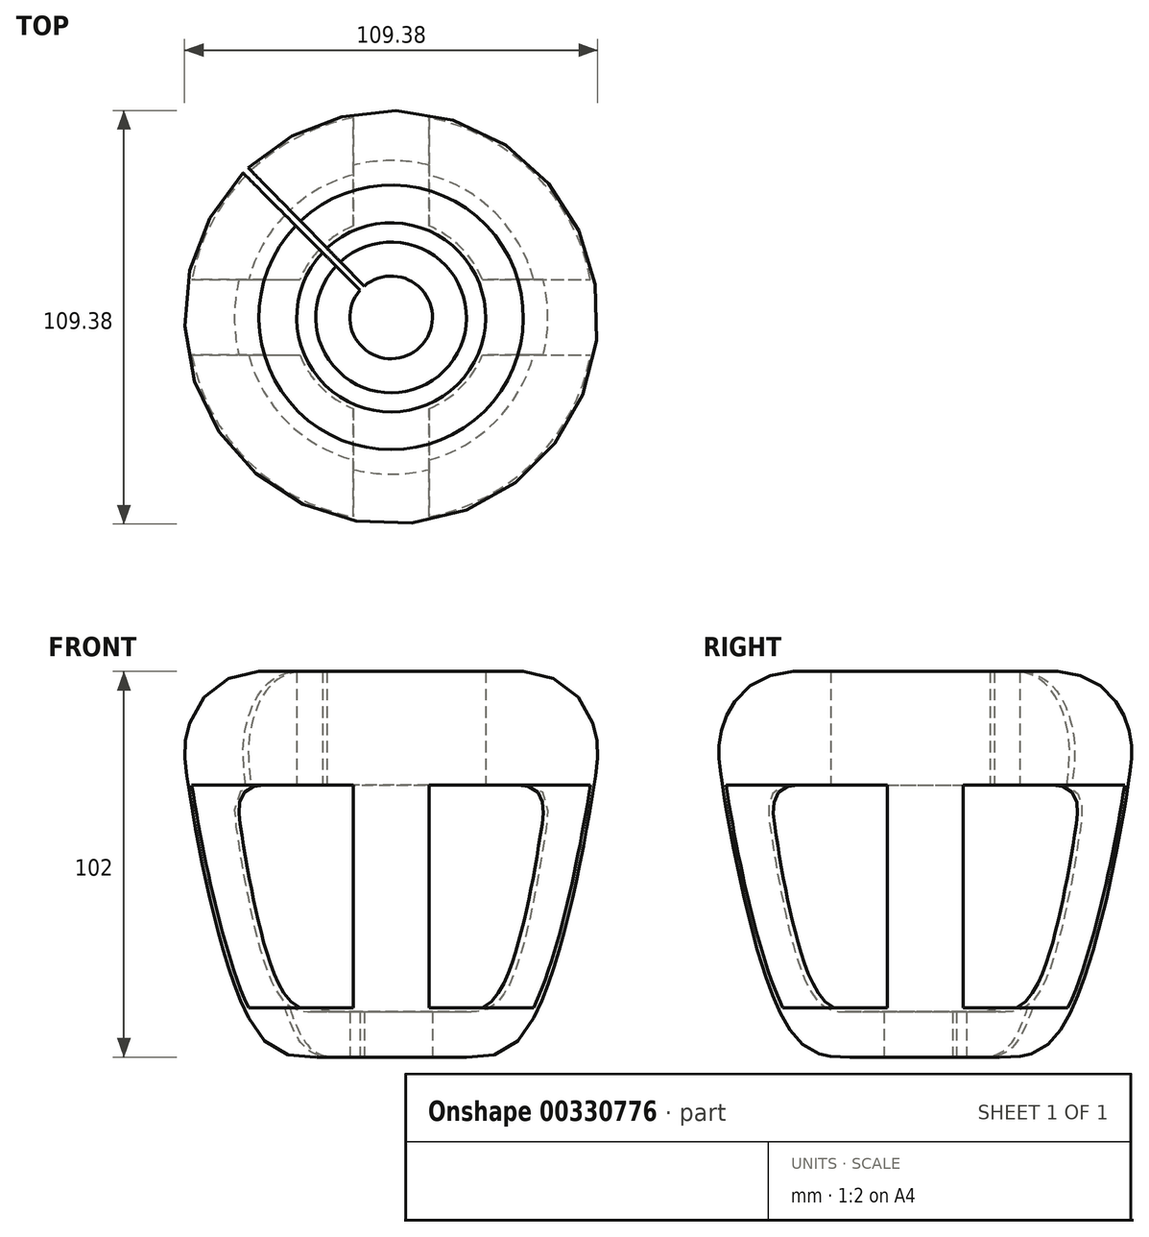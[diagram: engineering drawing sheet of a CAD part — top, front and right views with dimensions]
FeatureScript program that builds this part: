
annotation { "Feature Type Name" : "Feature", "Feature Type Description" : "" }
export const myFeature = defineFeature(function(context is Context, id is Id, definition is map)
    precondition{}
    {
        {
            var Q0;
            Q0=qCreatedBy(makeId("Front.planeOp"),FACE);
            var sketch = newSketch(context, id + "F0", { "sketchPlane" : qUnion([Q0])});
            skLineSegment(sketch, "E0", {"start": v(19.94, 0) * mm, "end": v(19.94, 12) * mm});
            skLineSegment(sketch, "E1", {"start": v(0, 12) * mm, "end": v(0, 72) * mm});
            skLineSegment(sketch, "E2", {"start": v(35, 72) * mm, "end": v(35, 102) * mm});
            skLineSegment(sketch, "E3", {"start": v(0, 0) * mm, "end": v(0, 122.17) * mm, "construction": true});
            skPoint(sketch, "E4.1.internal.snap0", {"position": v(35, 87) * mm});
            skPoint(sketch, "E4.3.internal.snap0", {"position": v(19.94, 6) * mm});
            skFitSpline(sketch, "E4", {"points": [v(35, 102) * mm, v(53.76, 87) * mm, v(53.7, 72) * mm, v(35, 6) * mm, v(19.94, 0) * mm], "startDerivative": vector(163.57, -9.42) * mm, "endDerivative": vector(-83.47, -0.77) * mm});
            skFitSpline(sketch, "E5", {"points": [v(35, 72) * mm, v(40.9, 59.77) * mm, v(37.46, 40.18) * mm, v(29.27, 15.77) * mm, v(19.94, 12) * mm], "startDerivative": vector(103.2, -2.48) * mm, "endDerivative": vector(-64.73, 3.98) * mm});
            skLineSegment(sketch, "E6", {"start": v(19.94, 12) * mm, "end": v(10.94, 12) * mm});
            skLineSegment(sketch, "E7", {"start": v(10.94, 12) * mm, "end": v(10.94, 0) * mm});
            skLineSegment(sketch, "E8", {"start": v(10.94, 0) * mm, "end": v(19.94, 0) * mm});
            skLineSegment(sketch, "E9", {"start": v(35, 102) * mm, "end": v(25, 102) * mm});
            skLineSegment(sketch, "E10", {"start": v(25, 102) * mm, "end": v(25, 72) * mm});
            skLineSegment(sketch, "E11", {"start": v(25, 72) * mm, "end": v(35, 72) * mm});
            skSolve(sketch);
        }
        {
            var Q0;
            Q0=makeQuery(id+"F0.imprint","IMPRINT",FACE,{"disambiguationData":[TD([[makeQuery(id+"F0.imprint","IMPRINT",EDGE,{"derivedFrom":sQuery(id+"F0.wireOp",EDGE,"E2")}),1.0]])]});
            var Q1;
            Q1=makeQuery(id+"F0.imprint","IMPRINT",FACE,{"disambiguationData":[TD([[makeQuery(id+"F0.imprint","IMPRINT",EDGE,{"derivedFrom":sQuery(id+"F0.wireOp",EDGE,"E0")}),-1.0]])]});
            var Q2;
            Q2=makeQuery(id+"F0.imprint","IMPRINT",FACE,{"disambiguationData":[TD([[makeQuery(id+"F0.imprint","IMPRINT",EDGE,{"derivedFrom":sQuery(id+"F0.wireOp",EDGE,"E0")}),1.0]])]});
            var Q3;
            Q3=sQuery(id+"F0.wireOp",EDGE,"E3");
            revolve(context, id + "F1", {"entities" : qUnion([Q0, Q1, Q2]), "axis" : qUnion([Q3]), "revolveType" : RevolveType.FULL});
        }
        {
            var Q0;
            Q0=qCreatedBy(makeId("Front.planeOp"),FACE);
            cPlane(context, id + "F2", {"entities" : qUnion([Q0]), "cplaneType" : CPlaneType.OFFSET, "offset" : 55 * mm, "width" : 150 * mm, "height" : 150 * mm});
        }
        {
            var Q0;
            Q0=qCreatedBy(id+"F2.planeOp",FACE);
            var sketch = newSketch(context, id + "F3", { "sketchPlane" : qUnion([Q0])});
            skLineSegment(sketch, "E12", {"start": v(0, 0) * mm, "end": v(0, 13) * mm});
            skLineSegment(sketch, "E13", {"start": v(0, 13) * mm, "end": v(10, 13) * mm});
            skLineSegment(sketch, "E14", {"start": v(10, 13) * mm, "end": v(10, 72) * mm});
            skLineSegment(sketch, "E15", {"start": v(10, 72) * mm, "end": v(62.7, 72) * mm});
            skLineSegment(sketch, "E16", {"start": v(62.7, 72) * mm, "end": v(62.7, 13) * mm});
            skLineSegment(sketch, "E17", {"start": v(62.7, 13) * mm, "end": v(10, 13) * mm});
            skLineSegment(sketch, "E18", {"start": v(0, 13) * mm, "end": v(-10, 13) * mm});
            skLineSegment(sketch, "E19", {"start": v(-10, 13) * mm, "end": v(-10, 72) * mm});
            skLineSegment(sketch, "E20", {"start": v(-10, 72) * mm, "end": v(-72.12, 72) * mm});
            skLineSegment(sketch, "E21", {"start": v(-72.12, 72) * mm, "end": v(-72.12, 13) * mm});
            skLineSegment(sketch, "E22", {"start": v(-72.12, 13) * mm, "end": v(-10, 13) * mm});
            skSolve(sketch);
        }
        {
            var Q0;
            Q0=makeQuery(id+"F3.imprint","IMPRINT",FACE,{"disambiguationData":[TD([[makeQuery(id+"F3.imprint","IMPRINT",EDGE,{"derivedFrom":sQuery(id+"F3.wireOp",EDGE,"E19")}),1.0]])]});
            var Q1;
            Q1=makeQuery(id+"F3.imprint","IMPRINT",FACE,{"disambiguationData":[TD([[makeQuery(id+"F3.imprint","IMPRINT",EDGE,{"derivedFrom":sQuery(id+"F3.wireOp",EDGE,"E14")}),-1.0]])]});
            extrude(context, id + "F4", {"entities" : qUnion([Q0, Q1]), "operationType" : NewBodyOperationType.REMOVE, "oppositeDirection" : true, "depth" : 45 * mm});
        }
        {
            var Q0;
            Q0=qCreatedBy(makeId("Front.planeOp"),FACE);
            cPlane(context, id + "F5", {"entities" : qUnion([Q0]), "cplaneType" : CPlaneType.OFFSET, "offset" : 55 * mm, "oppositeDirection" : true, "width" : 150 * mm, "height" : 150 * mm});
        }
        {
            var Q0;
            Q0=qCreatedBy(id+"F5.planeOp",FACE);
            var sketch = newSketch(context, id + "F6", { "sketchPlane" : qUnion([Q0])});
            skLineSegment(sketch, "E23", {"start": v(0, 0) * mm, "end": v(0, 13) * mm});
            skLineSegment(sketch, "E24", {"start": v(0, 13) * mm, "end": v(-10, 13) * mm});
            skLineSegment(sketch, "E25", {"start": v(-10, 13) * mm, "end": v(-10, 72) * mm});
            skLineSegment(sketch, "E26", {"start": v(-10, 72) * mm, "end": v(-78.5, 72) * mm});
            skLineSegment(sketch, "E27", {"start": v(-78.5, 72) * mm, "end": v(-78.5, 13) * mm});
            skLineSegment(sketch, "E28", {"start": v(-78.5, 13) * mm, "end": v(-10, 13) * mm});
            skLineSegment(sketch, "E29", {"start": v(0, 13) * mm, "end": v(10, 13) * mm});
            skLineSegment(sketch, "E30", {"start": v(10, 13) * mm, "end": v(10, 72) * mm});
            skLineSegment(sketch, "E31", {"start": v(10, 72) * mm, "end": v(73.5, 72) * mm});
            skLineSegment(sketch, "E32", {"start": v(73.5, 72) * mm, "end": v(73.5, 13) * mm});
            skLineSegment(sketch, "E33", {"start": v(73.5, 13) * mm, "end": v(10, 13) * mm});
            skSolve(sketch);
        }
        {
            var Q0;
            Q0=makeQuery(id+"F6.imprint","IMPRINT",FACE,{"disambiguationData":[TD([[makeQuery(id+"F6.imprint","IMPRINT",EDGE,{"derivedFrom":sQuery(id+"F6.wireOp",EDGE,"E30")}),-1.0]])]});
            var Q1;
            Q1=makeQuery(id+"F6.imprint","IMPRINT",FACE,{"disambiguationData":[TD([[makeQuery(id+"F6.imprint","IMPRINT",EDGE,{"derivedFrom":sQuery(id+"F6.wireOp",EDGE,"E25")}),1.0]])]});
            extrude(context, id + "F7", {"entities" : qUnion([Q0, Q1]), "operationType" : NewBodyOperationType.REMOVE, "depth" : 45 * mm});
        }
        {
            var Q0;
            Q0=makeQuery(id+"F1.opRevolve","SWEPT_FACE",FACE,{"disambiguationData":[OSD([sQuery(id+"F0.wireOp",EDGE,"E9")])]});
            var sketch = newSketch(context, id + "F8", { "sketchPlane" : qUnion([Q0])});
            skLineSegment(sketch, "E34", {"start": v(0, 0) * mm, "end": v(0, 1) * mm});
            skLineSegment(sketch, "E35", {"start": v(0, 0) * mm, "end": v(-1, 0) * mm});
            skLineSegment(sketch, "E36", {"start": v(0, 1) * mm, "end": v(-1, 0) * mm});
            skLineSegment(sketch, "E37", {"start": v(-1, 0) * mm, "end": v(-42.21, 41.21) * mm});
            skLineSegment(sketch, "E38", {"start": v(-42.21, 41.21) * mm, "end": v(-40.8, 42.63) * mm});
            skLineSegment(sketch, "E39", {"start": v(-40.8, 42.63) * mm, "end": v(0, 1) * mm});
            skSolve(sketch);
        }
        {
            var Q0;
            Q0=makeQuery(id+"F8.imprint","IMPRINT",FACE,{"disambiguationData":[TD([[makeQuery(id+"F8.imprint","IMPRINT",EDGE,{"derivedFrom":sQuery(id+"F8.wireOp",EDGE,"E34")}),1.0]])]});
            var Q1;
            {var subQ0=sQuery(id+"F8.wireOp",EDGE,"E38");Q1=makeQuery(id+"F8.imprint","IMPRINT",FACE,{"disambiguationData":[TD([[makeQuery(id+"F8.imprint","IMPRINT",EDGE,{"derivedFrom":subQ0}),-1.0]])]});}
            var Q2;
            {var subQ0=sQuery(id+"F8.wireOp",EDGE,"E37");var subQ1=sQuery(id+"F0.wireOp",EDGE,"E9");var subQ4=makeQuery(id+"F1.opRevolve","SWEPT_EDGE",EDGE,{"disambiguationData":[OSD([subQ1,sQuery(id+"F0.wireOp",EDGE,"E10")])]});var subQ5=makeQuery(id+"F8.imprint","INTERSECT",VERTEX,{"derivedFrom":[subQ4,subQ0]});Q2=makeQuery(id+"F8.imprint","IMPRINT",FACE,{"disambiguationData":[TD([[makeQuery(id+"F8.imprint","IMPRINT",EDGE,{"disambiguationData":[TD([[subQ5,-1.0]])],"derivedFrom":subQ0}),-1.0]])]});}
            var Q3;
            {var subQ0=sQuery(id+"F8.wireOp",EDGE,"E36");Q3=makeQuery(id+"F8.imprint","IMPRINT",FACE,{"disambiguationData":[TD([[makeQuery(id+"F8.imprint","IMPRINT",EDGE,{"derivedFrom":subQ0}),-1.0]])]});}
            extrude(context, id + "F9", {"entities" : qUnion([Q0, Q1, Q2, Q3]), "operationType" : NewBodyOperationType.REMOVE, "oppositeDirection" : true, "depth" : 120 * mm});
        }
    });
